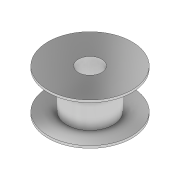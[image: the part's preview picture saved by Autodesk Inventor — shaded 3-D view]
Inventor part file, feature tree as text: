
AUTODESK INVENTOR PART (.ipt)
format: ipt  version: 2020 (Build 240168000, 168)  size: 107,520 bytes
history: native  units: in
note: dims shown in document units (in); Inventor stores cm internally (conversion verified against a paired STEP export)
features: extrude x3, sketch x3
ambient origin geometry x8: Origin, YZ Plane, XZ Plane, XY Plane, X Axis, Y Axis, Z Axis, Center Point
bodies: Solid1 (feature_tree)
feature tree (6):
  extrude  "Extrusion1"  Depth=0.1969in
  extrude  "Extrusion2"  Depth=0.3937in
  extrude  "Extrusion3"  Depth=0.0197in TaperAngle=0.0deg
  sketch  "Sketch1"  dims[d0=0.7087in d1=0.1969in]
  sketch  "Sketch2"  dims[d2=0.0197in d3=0.0in d4=0.3937in]
  sketch  "Sketch3"  dims[d5=0.315in d6=0.0in d7=0.0197in d8=0.0in]
